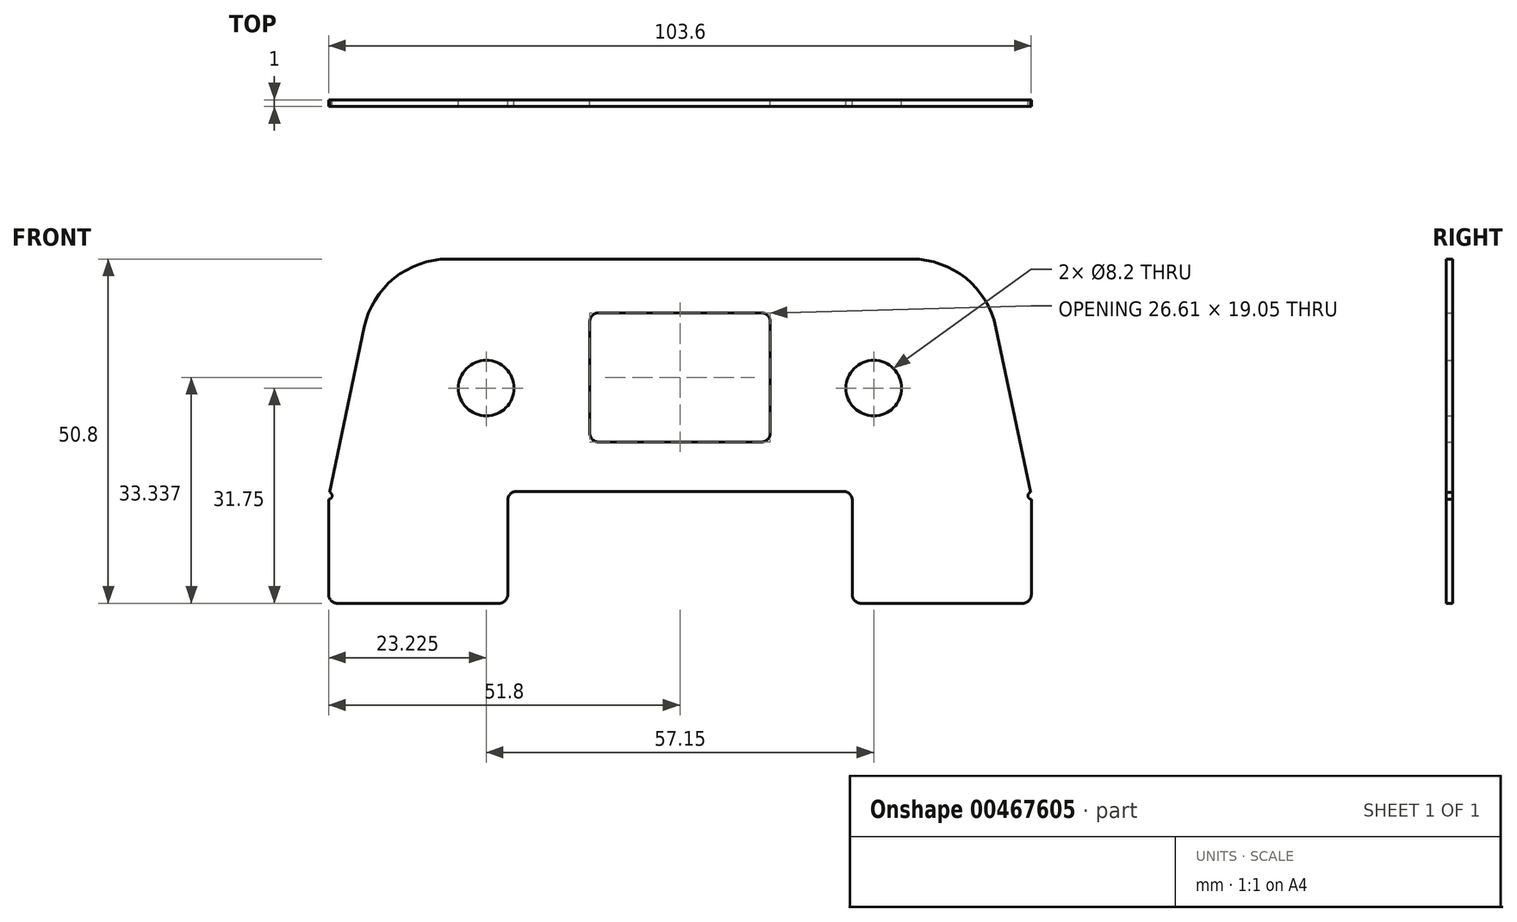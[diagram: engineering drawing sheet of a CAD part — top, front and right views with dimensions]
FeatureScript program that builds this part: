
annotation { "Feature Type Name" : "Feature", "Feature Type Description" : "" }
export const myFeature = defineFeature(function(context is Context, id is Id, definition is map)
    precondition{}
    {
        {
            var Q0;
            Q0=qCreatedBy(makeId("Front.planeOp"),FACE);
            var sketch = newSketch(context, id + "F0", { "sketchPlane" : qUnion([Q0])});
            skLineSegment(sketch, "E0", {"start": v(0, 0) * mm, "end": v(-28.58, 0) * mm, "construction": true});
            skCircle(sketch, "E1", {"center": v(-28.58, 0) * mm, "radius": 4.1 * mm});
            skLineSegment(sketch, "E2", {"start": v(0, 19.05) * mm, "end": v(-34.15, 19.05) * mm});
            skLineSegment(sketch, "E3", {"start": v(-46.57, 8.97) * mm, "end": v(-51.7, -15.38) * mm});
            skLineSegment(sketch, "E4", {"start": v(-50.53, -31.75) * mm, "end": v(-26.67, -31.75) * mm});
            skLineSegment(sketch, "E5", {"start": v(0, 0) * mm, "end": v(0, 19.05) * mm, "construction": true});
            skLineSegment(sketch, "E6", {"start": v(0, 0) * mm, "end": v(0, -31.75) * mm, "construction": true});
            skLineSegment(sketch, "E7", {"start": v(0, -15.87) * mm, "end": v(-51.8, -15.88) * mm, "construction": true});
            skArc(sketch, "E8", {"start": v(-51.8, -16.38) * mm, "mid": v(-51.3, -15.93) * mm, "end": v(-51.7, -15.38) * mm});
            skPoint(sketch, "E9.visualSharp", {"position": v(-44.45, 19.05) * mm});
            skArc(sketch, "E9.filletArc", {"start": v(-34.15, 19.05) * mm, "mid": v(-42.15, 16.21) * mm, "end": v(-46.57, 8.97) * mm});
            skLineSegment(sketch, "E10", {"start": v(-12.04, -7.94) * mm, "end": v(0, -7.94) * mm});
            skLineSegment(sketch, "E11", {"start": v(0, 11.11) * mm, "end": v(-12.04, 11.11) * mm});
            skLineSegment(sketch, "E12", {"start": v(-13.3, 9.84) * mm, "end": v(-13.3, -6.67) * mm});
            skPoint(sketch, "E13.visualSharp", {"position": v(-13.3, 11.11) * mm});
            skArc(sketch, "E13.filletArc", {"start": v(-12.04, 11.11) * mm, "mid": v(-12.93, 10.74) * mm, "end": v(-13.3, 9.84) * mm});
            skLineSegment(sketch, "E14.MirrorCS", {"start": v(0, 19.05) * mm, "end": v(34.15, 19.05) * mm});
            skArc(sketch, "E15.MirrorCS", {"start": v(34.15, 19.05) * mm, "mid": v(42.15, 16.21) * mm, "end": v(46.57, 8.97) * mm});
            skLineSegment(sketch, "E16.MirrorCS", {"start": v(46.57, 8.97) * mm, "end": v(51.7, -15.38) * mm});
            skLineSegment(sketch, "E17.MirrorCS", {"start": v(12.04, -7.94) * mm, "end": v(0, -7.94) * mm});
            skLineSegment(sketch, "E18.MirrorCS", {"start": v(13.3, 9.84) * mm, "end": v(13.3, -6.67) * mm});
            skLineSegment(sketch, "E19.MirrorCS", {"start": v(0, 11.11) * mm, "end": v(12.04, 11.11) * mm});
            skCircle(sketch, "E20.MirrorC", {"center": v(28.58, 0) * mm, "radius": 4.1 * mm});
            skArc(sketch, "E21.MirrorCS", {"start": v(12.04, 11.11) * mm, "mid": v(12.93, 10.74) * mm, "end": v(13.3, 9.84) * mm});
            skLineSegment(sketch, "E22", {"start": v(-25.4, -30.48) * mm, "end": v(-25.4, -16.5) * mm});
            skPoint(sketch, "E23.MirrorCS.end.orphan", {"position": v(0, -31.75) * mm});
            skPoint(sketch, "E24.visualSharp", {"position": v(-25.4, -31.75) * mm});
            skArc(sketch, "E24.filletArc", {"start": v(-26.67, -31.75) * mm, "mid": v(-25.77, -31.38) * mm, "end": v(-25.4, -30.48) * mm});
            skArc(sketch, "E25.MirrorCS", {"start": v(26.67, -31.75) * mm, "mid": v(25.77, -31.38) * mm, "end": v(25.4, -30.48) * mm});
            skPoint(sketch, "E26.visualSharp", {"position": v(-13.3, -7.94) * mm});
            skArc(sketch, "E26.filletArc", {"start": v(-13.3, -6.67) * mm, "mid": v(-12.93, -7.57) * mm, "end": v(-12.04, -7.94) * mm});
            skPoint(sketch, "E27.visualSharp", {"position": v(13.3, -7.94) * mm});
            skArc(sketch, "E27.filletArc", {"start": v(12.04, -7.94) * mm, "mid": v(12.93, -7.57) * mm, "end": v(13.3, -6.67) * mm});
            skCircle(sketch, "E28", {"center": v(-28.58, 0) * mm, "radius": 7.33 * mm, "construction": true});
            skLineSegment(sketch, "E29", {"start": v(-32.24, -6.35) * mm, "end": v(-35.9, 0) * mm, "construction": true});
            skLineSegment(sketch, "E30", {"start": v(-35.9, 0) * mm, "end": v(-32.24, 6.35) * mm, "construction": true});
            skLineSegment(sketch, "E31", {"start": v(-32.24, 6.35) * mm, "end": v(-24.9, 6.35) * mm});
            skLineSegment(sketch, "E32", {"start": v(-24.9, 6.35) * mm, "end": v(-21.24, 0) * mm, "construction": true});
            skLineSegment(sketch, "E33", {"start": v(-21.24, 0) * mm, "end": v(-24.9, -6.35) * mm, "construction": true});
            skLineSegment(sketch, "E34", {"start": v(-24.9, -6.35) * mm, "end": v(-32.24, -6.35) * mm, "construction": true});
            skLineSegment(sketch, "E35", {"start": v(-51.8, -15.88) * mm, "end": v(-57.15, -41.27) * mm, "construction": true});
            skLineSegment(sketch, "E36", {"start": v(-51.8, -15.88) * mm, "end": v(-51.8, -30.48) * mm});
            skPoint(sketch, "E37.visualSharp", {"position": v(-51.8, -31.75) * mm});
            skArc(sketch, "E37.filletArc", {"start": v(-51.8, -30.48) * mm, "mid": v(-51.43, -31.38) * mm, "end": v(-50.53, -31.75) * mm});
            skArc(sketch, "E38.MirrorCS", {"start": v(51.8, -30.48) * mm, "mid": v(51.43, -31.38) * mm, "end": v(50.53, -31.75) * mm});
            skLineSegment(sketch, "E39.MirrorCS", {"start": v(51.8, -16.38) * mm, "end": v(51.8, -30.48) * mm});
            skLineSegment(sketch, "E40.MirrorCS", {"start": v(50.53, -31.75) * mm, "end": v(26.67, -31.75) * mm});
            skArc(sketch, "E41.MirrorCS", {"start": v(51.8, -16.38) * mm, "mid": v(51.3, -15.93) * mm, "end": v(51.7, -15.38) * mm});
            skPoint(sketch, "E42.orphan", {"position": v(51.8, -15.88) * mm});
            skLineSegment(sketch, "E43", {"start": v(-24.13, -15.24) * mm, "end": v(0, -15.24) * mm});
            skPoint(sketch, "E44.visualSharp", {"position": v(-25.4, -15.24) * mm});
            skArc(sketch, "E44.filletArc", {"start": v(-24.13, -15.24) * mm, "mid": v(-25.03, -15.61) * mm, "end": v(-25.4, -16.5) * mm});
            skLineSegment(sketch, "E45.MirrorCS", {"start": v(24.13, -15.24) * mm, "end": v(0, -15.24) * mm});
            skArc(sketch, "E46.MirrorCS", {"start": v(24.13, -15.24) * mm, "mid": v(25.03, -15.61) * mm, "end": v(25.4, -16.5) * mm});
            skLineSegment(sketch, "E47.MirrorCS", {"start": v(25.4, -30.48) * mm, "end": v(25.4, -16.5) * mm});
            skSolve(sketch);
        }
        {
            var Q0;
            Q0=makeQuery(id+"F0.imprint","IMPRINT",FACE,{"disambiguationData":[TD([[makeQuery(id+"F0.imprint","IMPRINT",EDGE,{"derivedFrom":sQuery(id+"F0.wireOp",EDGE,"E1")}),-1.0]])]});
            extrude(context, id + "F1", {"entities" : qUnion([Q0]), "depth" : 1 * mm});
        }
    });
